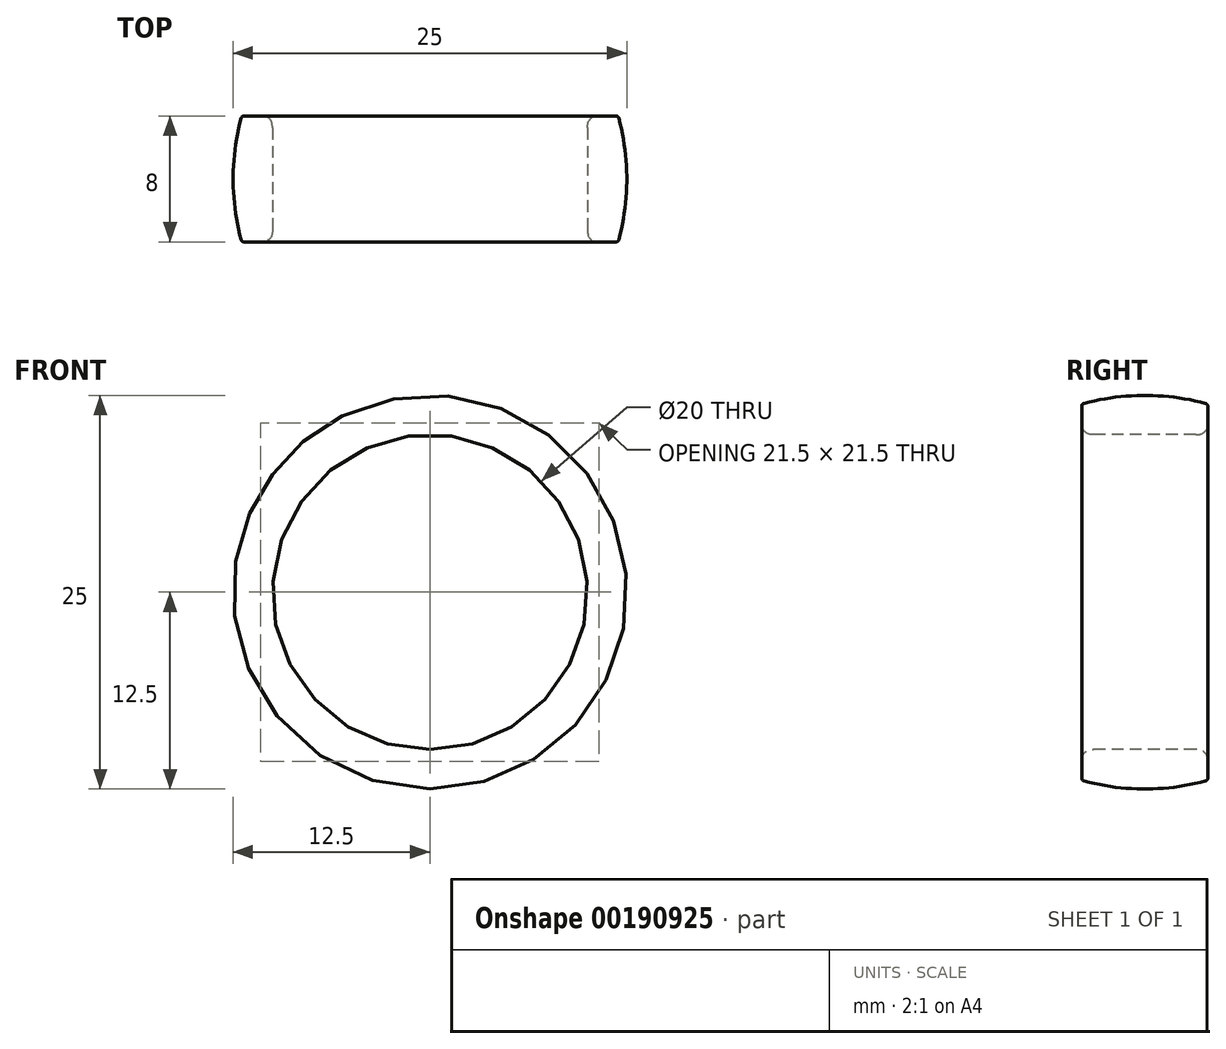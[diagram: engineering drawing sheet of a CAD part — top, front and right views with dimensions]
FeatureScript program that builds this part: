
annotation { "Feature Type Name" : "Feature", "Feature Type Description" : "" }
export const myFeature = defineFeature(function(context is Context, id is Id, definition is map)
    precondition{}
    {
        {
            var Q0;
            Q0=qCreatedBy(makeId("Front.planeOp"),FACE);
            var sketch = newSketch(context, id + "F0", { "sketchPlane" : qUnion([Q0])});
            skCircle(sketch, "E0", {"center": v(0, 0) * mm, "radius": 10 * mm});
            skCircle(sketch, "E1", {"center": v(0, 0) * mm, "radius": 12.5 * mm});
            skSolve(sketch);
        }
        {
            var Q0;
            Q0=qCreatedBy(makeId("Top.planeOp"),FACE);
            var sketch = newSketch(context, id + "F1", { "sketchPlane" : qUnion([Q0])});
            skLineSegment(sketch, "E2", {"start": v(-11.96, -4) * mm, "end": v(-10, -4) * mm});
            skLineSegment(sketch, "E3", {"start": v(-10, -4) * mm, "end": v(-10, 4) * mm});
            skLineSegment(sketch, "E4", {"start": v(-10, 4) * mm, "end": v(-11.96, 4) * mm});
            skLineSegment(sketch, "E5", {"start": v(-11.96, -4) * mm, "end": v(-11.96, 4) * mm, "construction": true});
            skArc(sketch, "E6", {"start": v(-11.96, 4) * mm, "mid": v(-12.5, 0) * mm, "end": v(-11.96, -4) * mm});
            skPoint(sketch, "E7", {"position": v(-10, 0) * mm});
            skPoint(sketch, "E8", {"position": v(-12.5, 0) * mm});
            skLineSegment(sketch, "E9", {"start": v(0, -7.75) * mm, "end": v(0, 6.8) * mm, "construction": true});
            skSolve(sketch);
        }
        {
            var Q0;
            Q0=makeQuery(id+"F1.imprint","IMPRINT",FACE,{"disambiguationData":[TD([[makeQuery(id+"F1.imprint","IMPRINT",EDGE,{"derivedFrom":sQuery(id+"F1.wireOp",EDGE,"E2")}),1.0]])]});
            var Q1;
            Q1=sQuery(id+"F1.wireOp",EDGE,"E9");
            revolve(context, id + "F2", {"entities" : qUnion([Q0]), "axis" : qUnion([Q1]), "revolveType" : RevolveType.FULL});
        }
        {
            var Q0;
            Q0=makeQuery(id+"F2.opRevolve","SWEPT_FACE",FACE,{"disambiguationData":[OSD([sQuery(id+"F1.wireOp",EDGE,"E6")])]});
            fillet(context, id + "F3", {"entities" : qUnion([Q0]), "radius" : 0.2 * mm, "tangentPropagation" : true, "rho" : 0.5, "crossSection" : FilletCrossSection.CONIC, "allowEdgeOverflow" : false});
        }
        {
            var Q0;
            Q0=makeQuery(id+"F2.opRevolve","SWEPT_FACE",FACE,{"disambiguationData":[OSD([sQuery(id+"F1.wireOp",EDGE,"E3")])]});
            fillet(context, id + "F4", {"entities" : qUnion([Q0]), "radius" : 0.75 * mm, "tangentPropagation" : true, "rho" : 0.5, "crossSection" : FilletCrossSection.CONIC, "allowEdgeOverflow" : false});
        }
    });
